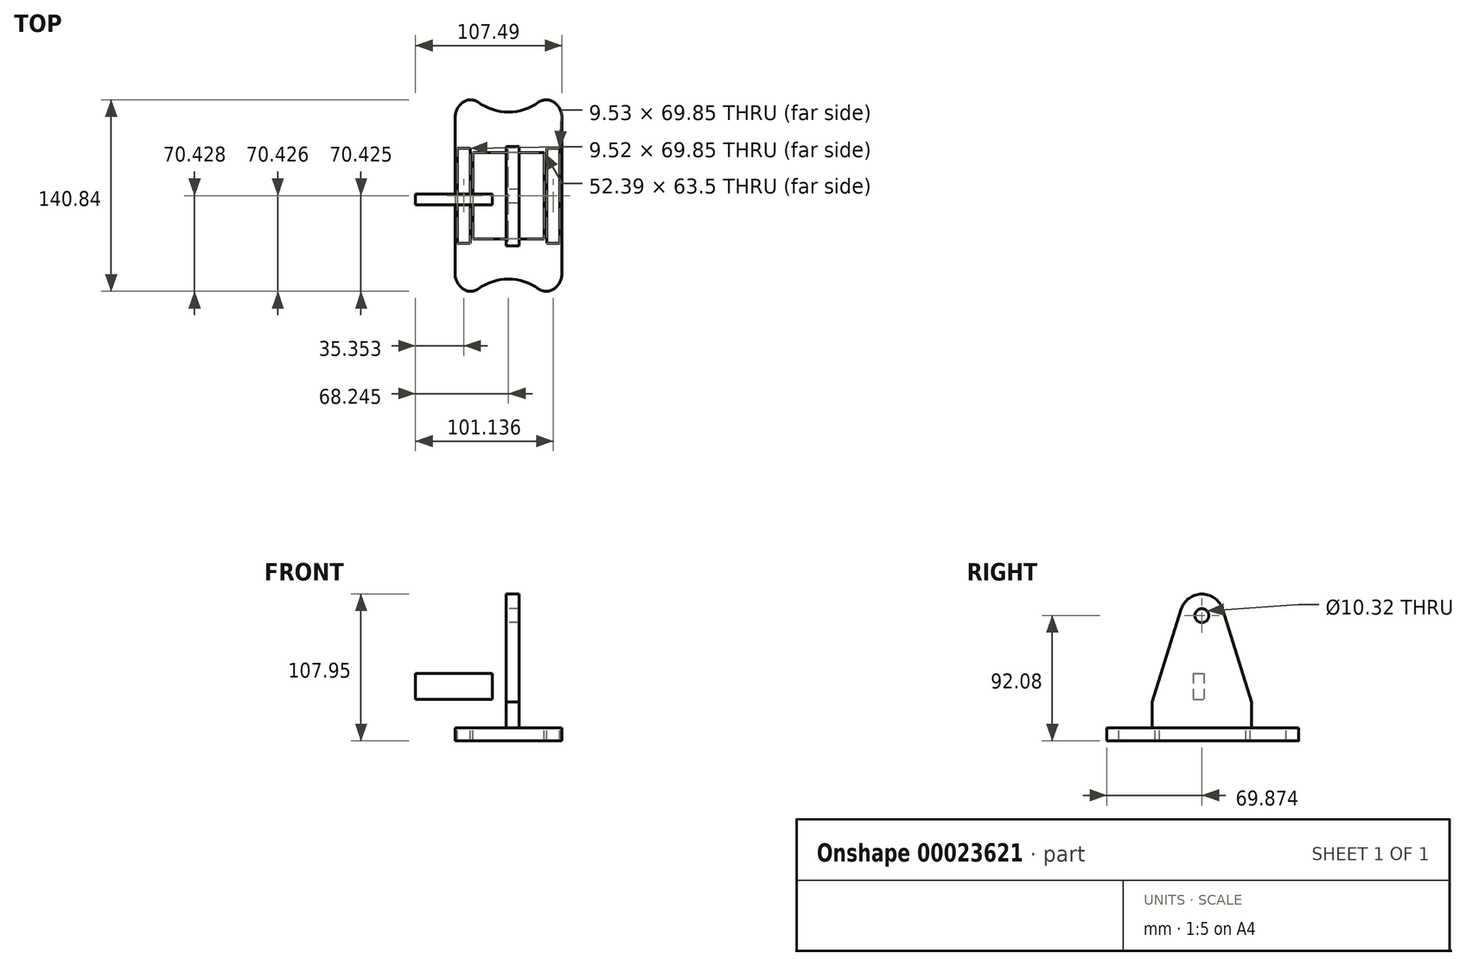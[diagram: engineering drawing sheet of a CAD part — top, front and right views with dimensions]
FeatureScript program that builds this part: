
annotation { "Feature Type Name" : "Feature", "Feature Type Description" : "" }
export const myFeature = defineFeature(function(context is Context, id is Id, definition is map)
    precondition{}
    {
        {
            var Q0;
            Q0=qCreatedBy(makeId("Right.planeOp"),FACE);
            var sketch = newSketch(context, id + "F0", { "sketchPlane" : qUnion([Q0])});
            skLineSegment(sketch, "E0", {"start": v(34.99, 19.05) * mm, "end": v(34.99, 0) * mm});
            skLineSegment(sketch, "E1", {"start": v(34.99, 0) * mm, "end": v(-38.04, 0) * mm});
            skLineSegment(sketch, "E2", {"start": v(34.99, 19.05) * mm, "end": v(-38.04, 19.05) * mm});
            skLineSegment(sketch, "E3", {"start": v(-38.04, 19.05) * mm, "end": v(-38.04, 0) * mm});
            skCircle(sketch, "E4", {"center": v(-1.53, 82.55) * mm, "radius": 15.88 * mm});
            skLineSegment(sketch, "E5", {"start": v(34.99, 19.05) * mm, "end": v(13.62, 87.3) * mm});
            skLineSegment(sketch, "E6", {"start": v(-16.68, 87.3) * mm, "end": v(-38.04, 19.05) * mm});
            skCircle(sketch, "E7", {"center": v(-1.53, 82.55) * mm, "radius": 5.16 * mm});
            skLineSegment(sketch, "E8", {"start": v(34.99, 0) * mm, "end": v(34.99, -9.53) * mm});
            skLineSegment(sketch, "E9", {"start": v(34.99, -9.53) * mm, "end": v(-38.04, -9.53) * mm});
            skLineSegment(sketch, "E10", {"start": v(-38.04, -9.53) * mm, "end": v(-38.04, 0) * mm});
            skSolve(sketch);
        }
        {
            var Q0;
            Q0=qCreatedBy(makeId("Top.planeOp"),FACE);
            var sketch = newSketch(context, id + "F1", { "sketchPlane" : qUnion([Q0])});
            skArc(sketch, "E11", {"start": v(40.82, 56.31) * mm, "mid": v(39.2, 62.83) * mm, "end": v(34.71, 67.82) * mm});
            skArc(sketch, "E12", {"start": v(-31.56, 67.82) * mm, "mid": v(-36.04, 62.84) * mm, "end": v(-37.67, 56.34) * mm});
            skLineSegment(sketch, "E13", {"start": v(-71.14, 70.18) * mm, "end": v(-71.14, -72.12) * mm});
            skLineSegment(sketch, "E14", {"start": v(-37.67, 35.54) * mm, "end": v(-10.68, 35.54) * mm});
            skLineSegment(sketch, "E15", {"start": v(40.82, 35.54) * mm, "end": v(13.83, 35.54) * mm});
            skLineSegment(sketch, "E16", {"start": v(-37.67, -37.48) * mm, "end": v(-10.68, -37.48) * mm});
            skLineSegment(sketch, "E17", {"start": v(40.82, -37.49) * mm, "end": v(13.83, -37.49) * mm});
            skLineSegment(sketch, "E18", {"start": v(-10.68, 35.54) * mm, "end": v(-10.68, -37.48) * mm});
            skLineSegment(sketch, "E19", {"start": v(13.83, 35.54) * mm, "end": v(13.83, -37.49) * mm});
            skLineSegment(sketch, "E20", {"start": v(-36.08, 33.95) * mm, "end": v(-36.08, -35.9) * mm});
            skLineSegment(sketch, "E21", {"start": v(-36.08, 33.95) * mm, "end": v(-26.55, 33.95) * mm});
            skLineSegment(sketch, "E22", {"start": v(-26.55, 33.95) * mm, "end": v(-26.55, -35.9) * mm});
            skLineSegment(sketch, "E23", {"start": v(-26.55, -35.9) * mm, "end": v(-36.08, -35.9) * mm});
            skPoint(sketch, "E24.start.orphan", {"position": v(-37.67, 33.95) * mm});
            skLineSegment(sketch, "E25", {"start": v(1.58, 60.48) * mm, "end": v(1.57, -72.13) * mm});
            skLineSegment(sketch, "E26.MirrorCS", {"start": v(39.23, 33.95) * mm, "end": v(29.7, 33.95) * mm});
            skLineSegment(sketch, "E27.MirrorCS", {"start": v(29.7, 33.95) * mm, "end": v(29.7, -35.9) * mm});
            skLineSegment(sketch, "E28.MirrorCS", {"start": v(39.23, 33.95) * mm, "end": v(39.23, -35.9) * mm});
            skLineSegment(sketch, "E29", {"start": v(29.7, -35.9) * mm, "end": v(39.23, -35.9) * mm});
            skArc(sketch, "E30", {"start": v(-20.67, 67.65) * mm, "mid": v(1.58, 60.48) * mm, "end": v(23.83, 67.65) * mm});
            skPoint(sketch, "E31.orphan", {"position": v(1.58, 70.18) * mm});
            skPoint(sketch, "E32.visualSharp", {"position": v(26.98, 70.18) * mm});
            skArc(sketch, "E32.filletArc", {"start": v(34.71, 67.82) * mm, "mid": v(29.24, 69.44) * mm, "end": v(23.83, 67.65) * mm});
            skPoint(sketch, "E33.visualSharp", {"position": v(-23.82, 70.18) * mm});
            skArc(sketch, "E33.filletArc", {"start": v(-20.67, 67.65) * mm, "mid": v(-26.09, 69.44) * mm, "end": v(-31.56, 67.82) * mm});
            skLineSegment(sketch, "E34", {"start": v(-37.67, -0.97) * mm, "end": v(82.74, -0.98) * mm});
            skPoint(sketch, "E35.MirrorP", {"position": v(-23.83, -72.13) * mm});
            skPoint(sketch, "E36.MirrorP", {"position": v(1.57, -72.13) * mm});
            skLineSegment(sketch, "E37", {"start": v(-37.67, 56.34) * mm, "end": v(-37.67, -0.97) * mm});
            skLineSegment(sketch, "E38", {"start": v(40.82, 56.31) * mm, "end": v(40.82, -0.98) * mm});
            skArc(sketch, "E39.MirrorCS", {"start": v(-31.57, -69.76) * mm, "mid": v(-36.05, -64.78) * mm, "end": v(-37.67, -58.28) * mm});
            skArc(sketch, "E40.MirrorCS", {"start": v(-20.68, -69.6) * mm, "mid": v(1.57, -62.43) * mm, "end": v(23.82, -69.6) * mm});
            skArc(sketch, "E41.MirrorCS", {"start": v(-20.68, -69.6) * mm, "mid": v(-26.1, -71.39) * mm, "end": v(-31.57, -69.76) * mm});
            skArc(sketch, "E42.MirrorCS", {"start": v(40.81, -58.27) * mm, "mid": v(39.2, -64.78) * mm, "end": v(34.7, -69.77) * mm});
            skPoint(sketch, "E43.MirrorP", {"position": v(26.97, -72.13) * mm});
            skArc(sketch, "E44.MirrorCS", {"start": v(34.7, -69.77) * mm, "mid": v(29.23, -71.4) * mm, "end": v(23.82, -69.6) * mm});
            skLineSegment(sketch, "E45", {"start": v(40.82, -0.98) * mm, "end": v(40.81, -58.27) * mm});
            skLineSegment(sketch, "E46", {"start": v(-37.67, -0.97) * mm, "end": v(-37.67, -58.28) * mm});
            skLineSegment(sketch, "E47", {"start": v(0, 0) * mm, "end": v(1.57, 0) * mm});
            skLineSegment(sketch, "E48", {"start": v(1.57, 0) * mm, "end": v(1.57, -0.97) * mm});
            skLineSegment(sketch, "E49", {"start": v(0, 0) * mm, "end": v(0, -0.97) * mm});
            skSolve(sketch);
        }
        {
            var Q0;
            Q0 = qSketchRegion(id + "F1", true);
            extrude(context, id + "F2", {"entities" : qUnion([Q0]), "oppositeDirection" : true, "depth" : 9.52 * mm});
        }
        {
            var Q0;
            Q0=makeQuery(id+"F0.imprint","IMPRINT",FACE,{"disambiguationData":[TD([[makeQuery(id+"F0.imprint","IMPRINT",EDGE,{"derivedFrom":sQuery(id+"F0.wireOp",EDGE,"E0")}),-1.0]])]});
            var Q1;
            Q1=makeQuery(id+"F0.imprint","IMPRINT",FACE,{"disambiguationData":[TD([[makeQuery(id+"F0.imprint","IMPRINT",EDGE,{"derivedFrom":sQuery(id+"F0.wireOp",EDGE,"E2")}),-1.0]])]});
            var Q2;
            Q2=makeQuery(id+"F0.imprint","IMPRINT",FACE,{"disambiguationData":[TD([[makeQuery(id+"F0.imprint","IMPRINT",EDGE,{"derivedFrom":sQuery(id+"F0.wireOp",EDGE,"E7")}),-1.0]])]});
            extrude(context, id + "F3", {"entities" : qUnion([Q0, Q1, Q2]), "depth" : 9.52 * mm});
        }
        {
            var Q0;
            Q0=makeQuery(id+"F2.opExtrude","CAP_FACE",FACE,{"disambiguationData":[OSD([sQuery(id+"F1.wireOp",EDGE,"E11"),sQuery(id+"F1.wireOp",EDGE,"E12"),sQuery(id+"F1.wireOp",EDGE,"E20"),sQuery(id+"F1.wireOp",EDGE,"E21"),sQuery(id+"F1.wireOp",EDGE,"E22"),sQuery(id+"F1.wireOp",EDGE,"E23"),sQuery(id+"F1.wireOp",EDGE,"E26.MirrorCS"),sQuery(id+"F1.wireOp",EDGE,"E27.MirrorCS"),sQuery(id+"F1.wireOp",EDGE,"E28.MirrorCS"),sQuery(id+"F1.wireOp",EDGE,"E29"),sQuery(id+"F1.wireOp",EDGE,"E30"),sQuery(id+"F1.wireOp",EDGE,"E32.filletArc"),sQuery(id+"F1.wireOp",EDGE,"E33.filletArc"),sQuery(id+"F1.wireOp",EDGE,"E37"),sQuery(id+"F1.wireOp",EDGE,"E38"),sQuery(id+"F1.wireOp",EDGE,"E39.MirrorCS"),sQuery(id+"F1.wireOp",EDGE,"E40.MirrorCS"),sQuery(id+"F1.wireOp",EDGE,"E41.MirrorCS"),sQuery(id+"F1.wireOp",EDGE,"E42.MirrorCS"),sQuery(id+"F1.wireOp",EDGE,"E44.MirrorCS"),sQuery(id+"F1.wireOp",EDGE,"E45"),sQuery(id+"F1.wireOp",EDGE,"E46")])],"isStart":true});
            var sketch = newSketch(context, id + "F4", { "sketchPlane" : qUnion([Q0])});
            skLineSegment(sketch, "E50", {"start": v(0, 0) * mm, "end": v(1.57, 0) * mm});
            skLineSegment(sketch, "E51", {"start": v(1.57, 0) * mm, "end": v(1.57, -0.97) * mm});
            skLineSegment(sketch, "E52.rect.bottom", {"start": v(27.77, 30.78) * mm, "end": v(-24.62, 30.78) * mm});
            skLineSegment(sketch, "E52.rect.top", {"start": v(27.77, -32.72) * mm, "end": v(-24.62, -32.72) * mm});
            skLineSegment(sketch, "E52.rect.left", {"start": v(27.77, 30.78) * mm, "end": v(27.77, -32.72) * mm});
            skLineSegment(sketch, "E52.rect.right", {"start": v(-24.62, 30.78) * mm, "end": v(-24.62, -32.72) * mm});
            skPoint(sketch, "E52.rect.middle", {"position": v(1.57, -0.97) * mm});
            skSolve(sketch);
        }
        {
            var Q0;
            Q0 = qSketchRegion(id + "F4", true);
            extrude(context, id + "F5", {"entities" : qUnion([Q0]), "operationType" : NewBodyOperationType.REMOVE, "oppositeDirection" : true, "depth" : 9.52 * mm});
        }
        {
            var Q0;
            Q0=qCreatedBy(makeId("Front.planeOp"),FACE);
            var sketch = newSketch(context, id + "F6", { "sketchPlane" : qUnion([Q0])});
            skLineSegment(sketch, "E53", {"start": v(-66.67, 40.17) * mm, "end": v(-10.4, 40.17) * mm});
            skLineSegment(sketch, "E54", {"start": v(-10.4, 40.17) * mm, "end": v(-10.4, 21.12) * mm});
            skLineSegment(sketch, "E55", {"start": v(-66.67, 40.17) * mm, "end": v(-66.67, 21.12) * mm});
            skLineSegment(sketch, "E56", {"start": v(-66.67, 21.12) * mm, "end": v(-10.4, 21.12) * mm});
            skSolve(sketch);
        }
        {
            var Q0;
            Q0=makeQuery(id+"F6.imprint","IMPRINT",FACE,{"disambiguationData":[TD([[makeQuery(id+"F6.imprint","IMPRINT",EDGE,{"derivedFrom":sQuery(id+"F6.wireOp",EDGE,"E53")}),-1.0]])]});
            extrude(context, id + "F7", {"entities" : qUnion([Q0]), "depth" : 7.94 * mm});
        }
    });
